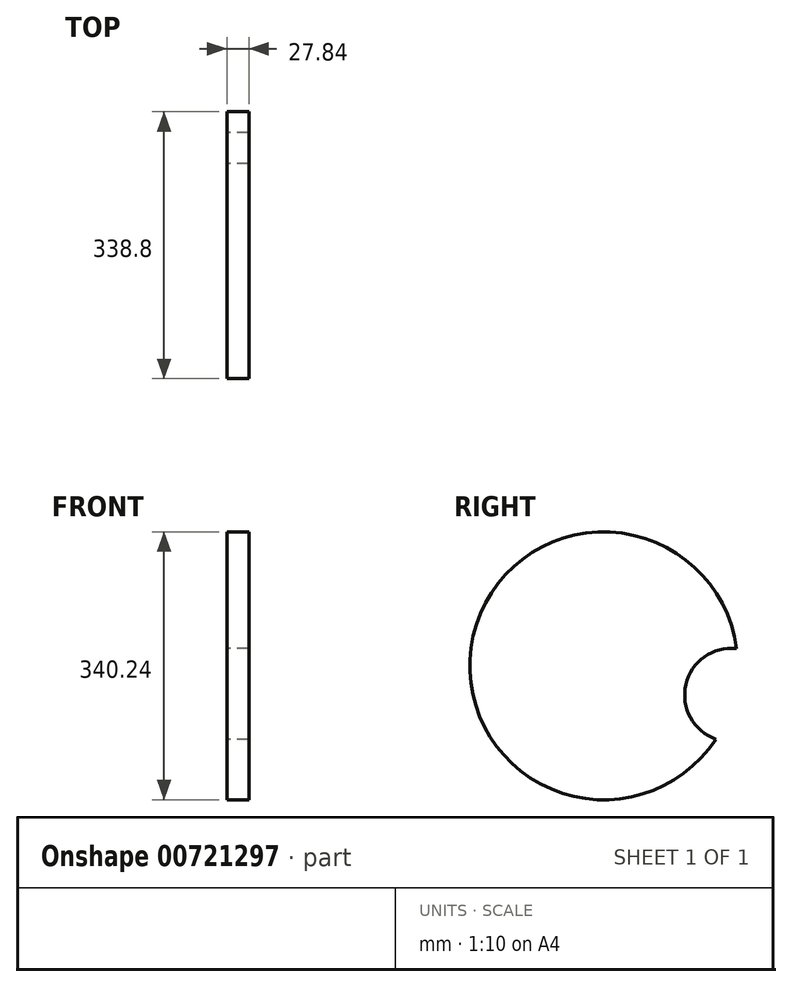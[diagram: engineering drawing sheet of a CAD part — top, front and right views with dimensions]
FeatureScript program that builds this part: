
annotation { "Feature Type Name" : "Feature", "Feature Type Description" : "" }
export const myFeature = defineFeature(function(context is Context, id is Id, definition is map)
    precondition{}
    {
        {
            var Q0;
            Q0=qCreatedBy(makeId("Right.planeOp"),FACE);
            var sketch = newSketch(context, id + "F0", { "sketchPlane" : qUnion([Q0])});
            skCircle(sketch, "E0", {"center": v(-46.46, 15.92) * mm, "radius": 170.12 * mm});
            skSolve(sketch);
        }
        {
            var Q0;
            Q0=makeQuery(id+"F0.imprint","IMPRINT",FACE,{"disambiguationData":[TD([[makeQuery(id+"F0.imprint","IMPRINT",EDGE,{"derivedFrom":sQuery(id+"F0.wireOp",EDGE,"E0")}),1.0]])]});
            extrude(context, id + "F1", {"entities" : qUnion([Q0]), "oppositeDirection" : true, "depth" : 27.84 * mm, "offsetDistance" : 25.4 * mm});
        }
        {
            var Q0;
            Q0=makeQuery(id+"F1.opExtrude","CAP_FACE",FACE,{"disambiguationData":[OSD([sQuery(id+"F0.wireOp",EDGE,"E0")])],"isStart":false});
            var sketch = newSketch(context, id + "F2", { "sketchPlane" : qUnion([Q0])});
            skArc(sketch, "E1", {"start": v(-95.9, -77.21) * mm, "mid": v(-57.93, -7.92) * mm, "end": v(-122.22, 38.03) * mm});
            skSolve(sketch);
        }
        {
            var Q0;
            {var subQ0=sQuery(id+"F2.wireOp",EDGE,"E1");Q0=makeQuery(id+"F2.imprint","IMPRINT",FACE,{"disambiguationData":[TD([[makeQuery(id+"F2.imprint","IMPRINT",EDGE,{"derivedFrom":subQ0}),1.0]])]});}
            extrude(context, id + "F3", {"entities" : qUnion([Q0]), "operationType" : NewBodyOperationType.REMOVE, "oppositeDirection" : true, "depth" : 74.22 * mm, "offsetDistance" : 25.4 * mm});
        }
    });
